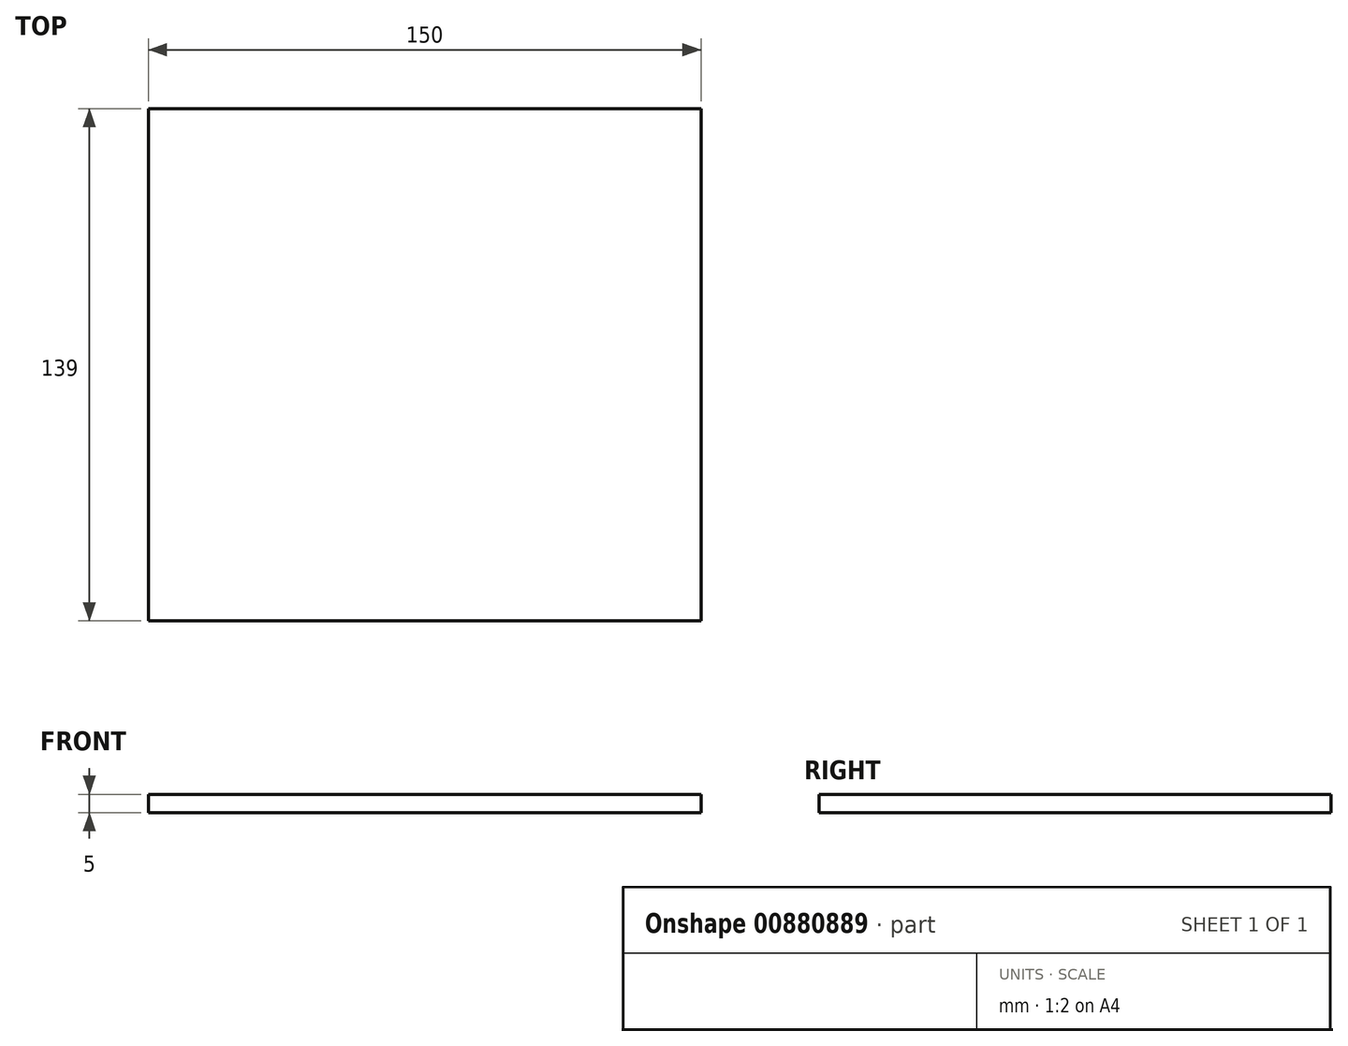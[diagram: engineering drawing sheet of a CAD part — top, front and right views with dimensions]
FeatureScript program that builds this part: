
annotation { "Feature Type Name" : "Feature", "Feature Type Description" : "" }
export const myFeature = defineFeature(function(context is Context, id is Id, definition is map)
    precondition{}
    {
        {
            var Q0;
            Q0=qCreatedBy(makeId("Top.planeOp"),FACE);
            var sketch = newSketch(context, id + "F0", { "sketchPlane" : qUnion([Q0])});
            skLineSegment(sketch, "E0.bottom", {"start": v(-93.2, 66.2) * mm, "end": v(56.8, 66.2) * mm});
            skLineSegment(sketch, "E0.top", {"start": v(-93.2, -72.8) * mm, "end": v(56.8, -72.8) * mm});
            skLineSegment(sketch, "E0.left", {"start": v(-93.2, 66.2) * mm, "end": v(-93.2, -72.8) * mm});
            skLineSegment(sketch, "E0.right", {"start": v(56.8, 66.2) * mm, "end": v(56.8, -72.8) * mm});
            skSolve(sketch);
        }
        {
            var Q0;
            Q0 = qSketchRegion(id + "F0", true);
            extrude(context, id + "F1", {"entities" : qUnion([Q0]), "depth" : 5 * mm, "offsetDistance" : 25 * mm});
        }
    });
